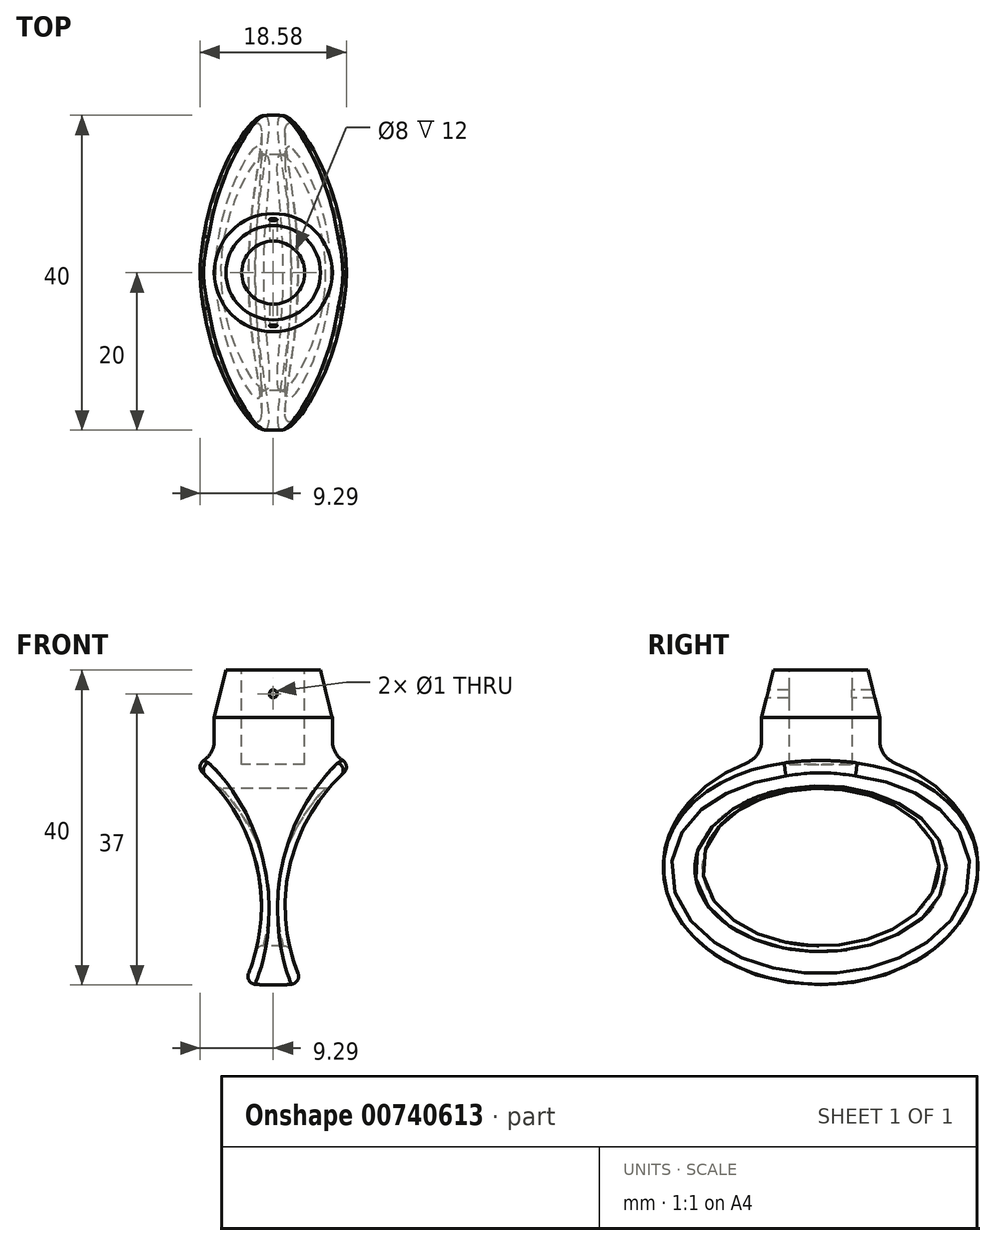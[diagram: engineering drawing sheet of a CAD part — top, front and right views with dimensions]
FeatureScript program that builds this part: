
annotation { "Feature Type Name" : "Feature", "Feature Type Description" : "" }
export const myFeature = defineFeature(function(context is Context, id is Id, definition is map)
    precondition{}
    {
        {
            var Q0;
            Q0=qCreatedBy(makeId("Front.planeOp"),FACE);
            var sketch = newSketch(context, id + "F0", { "sketchPlane" : qUnion([Q0])});
            skEllipticalArc(sketch, "E0", {});
            skLineSegment(sketch, "E1.top", {"start": v(6, 25) * mm, "end": v(0, 25) * mm});
            skLineSegment(sketch, "E1.left", {"start": v(7.5, 13.9) * mm, "end": v(7.5, 19) * mm});
            skPoint(sketch, "E1.middle", {"position": v(0, 18.48) * mm});
            skLineSegment(sketch, "E2", {"start": v(7.5, 19) * mm, "end": v(6, 25) * mm});
            skLineSegment(sketch, "E3", {"start": v(0, 25) * mm, "end": v(0, -15) * mm});
            skPoint(sketch, "E4.orphan", {"position": v(-7.5, 25) * mm});
            skPoint(sketch, "E1.right.start.orphan", {"position": v(-7.5, 11.96) * mm});
            skPoint(sketch, "E5.orphan", {"position": v(7.5, 11.96) * mm});
            skPoint(sketch, "E6.orphan", {"position": v(7.5, 25) * mm});
            const initialGuessF0  = {"E0": [0, 0, 1, 0, 0.02, 0.015, 4.71238898038469, 1.1863995522992579]};
            skSetInitialGuess(sketch, initialGuessF0);
            skSolve(sketch);
        }
        {
            var Q0;
            Q0=makeQuery(id+"F0.imprint","IMPRINT",FACE,{"disambiguationData":[TD([[makeQuery(id+"F0.imprint","IMPRINT",EDGE,{"derivedFrom":sQuery(id+"F0.wireOp",EDGE,"E0")}),1.0]])]});
            var Q1;
            Q1=sQuery(id+"F0.wireOp",EDGE,"E3");
            revolve(context, id + "F1", {"surfaceOperationType" : NewSurfaceOperationType.NEW, "entities" : qUnion([Q0]), "axis" : qUnion([Q1]), "revolveType" : RevolveType.FULL});
        }
        {
            var Q0;
            Q0=makeQuery(id+"F1.opRevolve","SWEPT_EDGE",EDGE,{"disambiguationData":[OSD([sQuery(id+"F0.wireOp",EDGE,"E0"),sQuery(id+"F0.wireOp",EDGE,"E1.left")])]});
            fillet(context, id + "F2", {"entities" : qUnion([Q0]), "radius" : 3 * mm, "tangentPropagation" : true, "allowEdgeOverflow" : false});
        }
        {
            var Q0;
            Q0=qCreatedBy(makeId("Front.planeOp"),FACE);
            var sketch = newSketch(context, id + "F3", { "sketchPlane" : qUnion([Q0])});
            skCircle(sketch, "E7", {"center": v(-24.5, -5) * mm, "radius": 23 * mm});
            skCircle(sketch, "E8.MirrorC", {"center": v(24.5, -5) * mm, "radius": 23 * mm});
            skSolve(sketch);
        }
        {
            var Q0;
            Q0 = qSketchRegion(id + "F3", true);
            extrude(context, id + "F4", {"entities" : qUnion([Q0]), "operationType" : NewBodyOperationType.REMOVE, "oppositeDirection" : true, "depth" : 25 * mm, "offsetDistance" : 25 * mm, "hasSecondDirection" : true, "secondDirectionOppositeDirection" : false, "secondDirectionDepth" : 25 * mm});
        }
        {
            var Q0;
            Q0=qCreatedBy(makeId("Right.planeOp"),FACE);
            var sketch = newSketch(context, id + "F5", { "sketchPlane" : qUnion([Q0])});
            skEllipse(sketch, "E9", {"center": v(0, 0) * mm, "majorRadius": 15 * mm, "minorRadius": 10 * mm, "majorAxis": v(1, 0)});
            skSolve(sketch);
        }
        {
            var Q0;
            Q0 = qSketchRegion(id + "F5", true);
            extrude(context, id + "F6", {"entities" : qUnion([Q0]), "operationType" : NewBodyOperationType.REMOVE, "oppositeDirection" : true, "depth" : 25 * mm, "offsetDistance" : 25 * mm, "hasSecondDirection" : true, "secondDirectionOppositeDirection" : false, "secondDirectionDepth" : 25 * mm});
        }
        {
            var Q0;
            Q0=makeQuery(id+"F4.boolean.opBoolean","INTERSECT",EDGE,{"derivedFrom":[makeQuery(id+"F1.opRevolve","SWEPT_FACE",FACE,{"disambiguationData":[OSD([sQuery(id+"F0.wireOp",EDGE,"E0")])]}),makeQuery(id+"F4.opExtrude","SWEPT_FACE",FACE,{"disambiguationData":[OSD([sQuery(id+"F3.wireOp",EDGE,"E7")])]})]});
            var Q1;
            Q1=makeQuery(id+"F6.boolean.opBoolean","INTERSECT",EDGE,{"derivedFrom":[makeQuery(id+"F4.boolean.opBoolean","COPY",FACE,{"derivedFrom":makeQuery(id+"F4.opExtrude","SWEPT_FACE",FACE,{"disambiguationData":[OSD([sQuery(id+"F3.wireOp",EDGE,"E7")])]})}),makeQuery(id+"F6.opExtrude","SWEPT_FACE",FACE,{"disambiguationData":[OSD([sQuery(id+"F5.wireOp",EDGE,"E9")])]})]});
            var Q2;
            Q2=makeQuery(id+"F4.boolean.opBoolean","INTERSECT",EDGE,{"derivedFrom":[makeQuery(id+"F1.opRevolve","SWEPT_FACE",FACE,{"disambiguationData":[OSD([sQuery(id+"F0.wireOp",EDGE,"E0")])]}),makeQuery(id+"F4.opExtrude","SWEPT_FACE",FACE,{"disambiguationData":[OSD([sQuery(id+"F3.wireOp",EDGE,"E8.MirrorC")])]})]});
            var Q3;
            Q3=makeQuery(id+"F6.boolean.opBoolean","INTERSECT",EDGE,{"derivedFrom":[makeQuery(id+"F4.boolean.opBoolean","COPY",FACE,{"derivedFrom":makeQuery(id+"F4.opExtrude","SWEPT_FACE",FACE,{"disambiguationData":[OSD([sQuery(id+"F3.wireOp",EDGE,"E8.MirrorC")])]})}),makeQuery(id+"F6.opExtrude","SWEPT_FACE",FACE,{"disambiguationData":[OSD([sQuery(id+"F5.wireOp",EDGE,"E9")])]})]});
            fillet(context, id + "F7", {"entities" : qUnion([Q0, Q1, Q2, Q3]), "radius" : 1 * mm, "tangentPropagation" : true, "allowEdgeOverflow" : false});
        }
        {
            var Q0;
            Q0=makeQuery(id+"F1.opRevolve","SWEPT_FACE",FACE,{"disambiguationData":[OSD([sQuery(id+"F0.wireOp",EDGE,"E1.top")])]});
            var sketch = newSketch(context, id + "F8", { "sketchPlane" : qUnion([Q0])});
            skCircle(sketch, "E10", {"center": v(0, 0) * mm, "radius": 4 * mm});
            skSolve(sketch);
        }
        {
            var Q0;
            Q0 = qSketchRegion(id + "F8", true);
            extrude(context, id + "F9", {"entities" : qUnion([Q0]), "operationType" : NewBodyOperationType.REMOVE, "oppositeDirection" : true, "depth" : 12 * mm, "offsetDistance" : 25 * mm});
        }
        {
            var Q0;
            Q0=qCreatedBy(makeId("Front.planeOp"),FACE);
            var sketch = newSketch(context, id + "F10", { "sketchPlane" : qUnion([Q0])});
            skCircle(sketch, "E11", {"center": v(0, 22) * mm, "radius": 0.5 * mm});
            skSolve(sketch);
        }
        {
            var Q0;
            Q0 = qSketchRegion(id + "F10", true);
            extrude(context, id + "F11", {"entities" : qUnion([Q0]), "operationType" : NewBodyOperationType.REMOVE, "endBound" : BoundingType.THROUGH_ALL, "oppositeDirection" : true, "depth" : 25 * mm, "offsetDistance" : 25 * mm, "hasSecondDirection" : true, "secondDirectionOppositeDirection" : false, "secondDirectionDepth" : 25 * mm});
        }
    });
